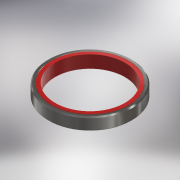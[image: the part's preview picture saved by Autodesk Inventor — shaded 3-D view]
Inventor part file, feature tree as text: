
AUTODESK INVENTOR PART (.ipt)
format: ipt  version: 2017 (Build 210142000, 142)  size: 149,504 bytes
history: native  units: mm
features: extrude x2, chamfer x2, sketch x2
ambient origin geometry x8: Origin, YZ Plane, XZ Plane, XY Plane, X Axis, Y Axis, Z Axis, Center Point
bodies: Solid1 (feature_tree), Solid2 (feature_tree)
feature tree (6):
  extrude  "Extrusion1"  Depth=7.0mm
  chamfer  "Chamfer1"  Distance=7.0mm
  extrude  "Extrusion2"  Depth=7.0mm
  chamfer  "Chamfer2"  Distance=7.0mm
  sketch  "Sketch1"  dims[d0=47.0mm d1=43.0mm d2=7.0mm d3=0.0mm]
  sketch  "Sketch2"  dims[d4=0.6mm d5=2.0mm d6=45.0deg d7=39.0mm d8=7.0mm d9=0.0mm d10=0.2mm d11=2.0mm d12=45.0deg]
